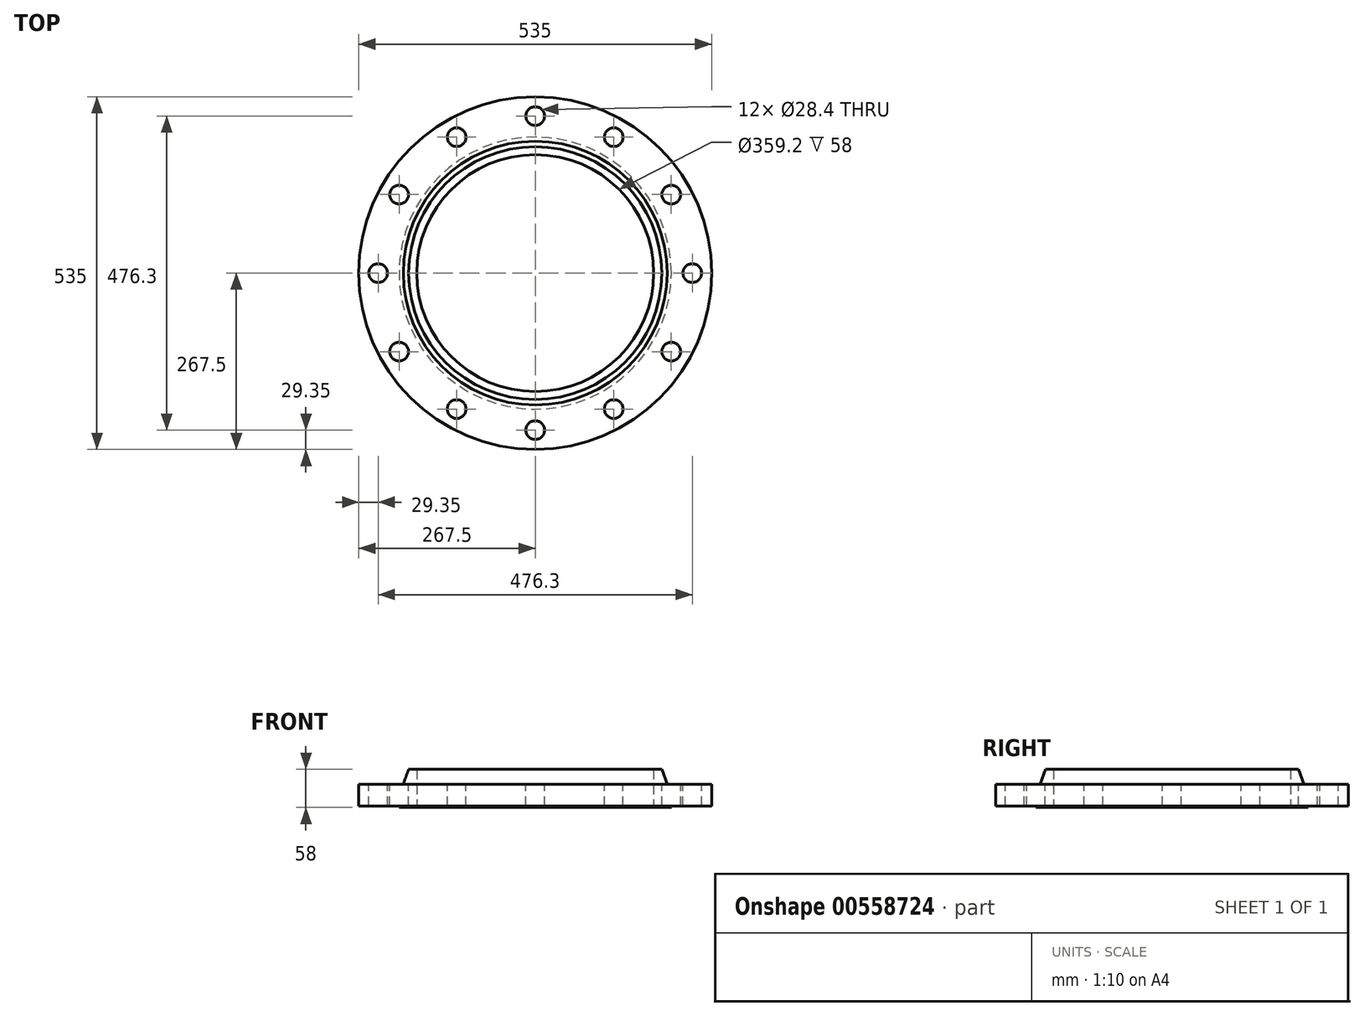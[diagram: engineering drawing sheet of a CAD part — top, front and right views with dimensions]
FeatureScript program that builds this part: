
annotation { "Feature Type Name" : "Feature", "Feature Type Description" : "" }
export const myFeature = defineFeature(function(context is Context, id is Id, definition is map)
    precondition{}
    {
        {
            var Q0;
            Q0=qCreatedBy(makeId("Front.planeOp"),FACE);
            var sketch = newSketch(context, id + "F0", { "sketchPlane" : qUnion([Q0])});
            skLineSegment(sketch, "E0", {"start": v(179.6, 0) * mm, "end": v(206.4, 0) * mm});
            skLineSegment(sketch, "E1", {"start": v(206.4, 0) * mm, "end": v(206.4, 2) * mm});
            skLineSegment(sketch, "E2", {"start": v(206.4, 2) * mm, "end": v(267.5, 2) * mm});
            skLineSegment(sketch, "E3", {"start": v(267.5, 2) * mm, "end": v(267.5, 35.4) * mm});
            skLineSegment(sketch, "E4", {"start": v(267.5, 35.4) * mm, "end": v(200, 35.4) * mm});
            skLineSegment(sketch, "E5", {"start": v(200, 35.4) * mm, "end": v(191.77, 58) * mm});
            skLineSegment(sketch, "E6", {"start": v(191.77, 58) * mm, "end": v(179.6, 58) * mm});
            skLineSegment(sketch, "E7", {"start": v(179.6, 58) * mm, "end": v(179.6, 0) * mm});
            skLineSegment(sketch, "E8", {"start": v(0, 0) * mm, "end": v(0, 58) * mm});
            skSolve(sketch);
        }
        {
            var Q0;
            Q0=makeQuery(id+"F0.imprint","IMPRINT",FACE,{"disambiguationData":[TD([[makeQuery(id+"F0.imprint","IMPRINT",EDGE,{"derivedFrom":sQuery(id+"F0.wireOp",EDGE,"E0")}),1.0]])]});
            var Q1;
            Q1=sQuery(id+"F0.wireOp",EDGE,"E8");
            revolve(context, id + "F1", {"entities" : qUnion([Q0]), "axis" : qUnion([Q1]), "revolveType" : RevolveType.FULL});
        }
        {
            var Q0;
            Q0=makeQuery(id+"F1.opRevolve","SWEPT_FACE",FACE,{"disambiguationData":[OSD([sQuery(id+"F0.wireOp",EDGE,"E4")])]});
            var sketch = newSketch(context, id + "F2", { "sketchPlane" : qUnion([Q0])});
            skCircle(sketch, "E9", {"center": v(0, 0) * mm, "radius": 238.15 * mm, "construction": true});
            skCircle(sketch, "E10", {"center": v(0, 238.15) * mm, "radius": 14.2 * mm});
            skCircle(sketch, "E11.1.0", {"center": v(-119.07, 206.24) * mm, "radius": 14.2 * mm});
            skCircle(sketch, "E11.2.0", {"center": v(-206.24, 119.08) * mm, "radius": 14.2 * mm});
            skCircle(sketch, "E11.3.0", {"center": v(-238.15, 0) * mm, "radius": 14.2 * mm});
            skCircle(sketch, "E11.4.0", {"center": v(-206.24, -119.07) * mm, "radius": 14.2 * mm});
            skCircle(sketch, "E11.5.0", {"center": v(-119.08, -206.24) * mm, "radius": 14.2 * mm});
            skCircle(sketch, "E11.6.0", {"center": v(0, -238.15) * mm, "radius": 14.2 * mm});
            skCircle(sketch, "E11.7.0", {"center": v(119.07, -206.24) * mm, "radius": 14.2 * mm});
            skCircle(sketch, "E11.8.0", {"center": v(206.24, -119.08) * mm, "radius": 14.2 * mm});
            skCircle(sketch, "E11.9.0", {"center": v(238.15, 0) * mm, "radius": 14.2 * mm});
            skCircle(sketch, "E11.10.0", {"center": v(206.24, 119.07) * mm, "radius": 14.2 * mm});
            skCircle(sketch, "E11.11.0", {"center": v(119.07, 206.24) * mm, "radius": 14.2 * mm});
            skSolve(sketch);
        }
        {
            var Q0;
            Q0 = qSketchRegion(id + "F2", true);
            extrude(context, id + "F3", {"entities" : qUnion([Q0]), "operationType" : NewBodyOperationType.REMOVE, "endBound" : BoundingType.THROUGH_ALL, "oppositeDirection" : true, "depth" : 25 * mm, "offsetDistance" : 25 * mm});
        }
    });
